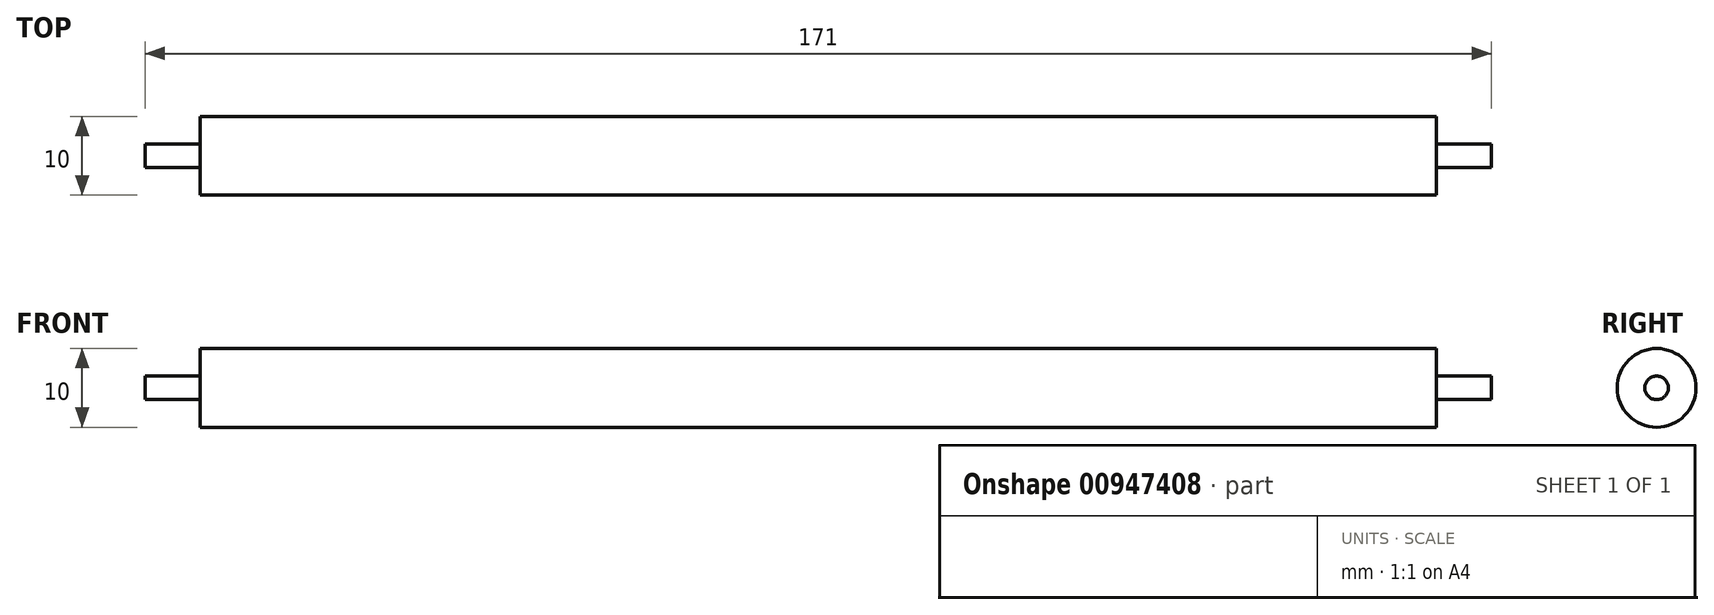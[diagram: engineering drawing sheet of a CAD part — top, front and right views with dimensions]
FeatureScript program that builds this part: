
annotation { "Feature Type Name" : "Feature", "Feature Type Description" : "" }
export const myFeature = defineFeature(function(context is Context, id is Id, definition is map)
    precondition{}
    {
        {
            var Q0;
            Q0=qCreatedBy(makeId("Right.planeOp"),FACE);
            var sketch = newSketch(context, id + "F0", { "sketchPlane" : qUnion([Q0])});
            skCircle(sketch, "E0", {"center": v(0, 0) * mm, "radius": 5 * mm});
            skSolve(sketch);
        }
        {
            var Q0;
            Q0 = qSketchRegion(id + "F0", true);
            var Q1;
            Q1=makeQuery(id+"F0.imprint","IMPRINT",FACE,{"disambiguationData":[TD([[makeQuery(id+"F0.imprint","IMPRINT",EDGE,{"derivedFrom":sQuery(id+"F0.wireOp",EDGE,"E0")}),1.0]])]});
            extrude(context, id + "F1", {"entities" : qUnion([Q0, Q1]), "depth" : 78.5 * mm, "offsetDistance" : 25.4 * mm});
        }
        {
            var Q0;
            Q0=makeQuery(id+"F1.opExtrude","CAP_FACE",FACE,{"disambiguationData":[OSD([sQuery(id+"F0.wireOp",EDGE,"E0")])],"isStart":false});
            var sketch = newSketch(context, id + "F2", { "sketchPlane" : qUnion([Q0])});
            skCircle(sketch, "E1", {"center": v(0, 0) * mm, "radius": 1.5 * mm});
            skSolve(sketch);
        }
        {
            var Q0;
            Q0=makeQuery(id+"F2.imprint","IMPRINT",FACE,{"disambiguationData":[TD([[makeQuery(id+"F2.imprint","IMPRINT",EDGE,{"derivedFrom":sQuery(id+"F2.wireOp",EDGE,"E1")}),1.0]])]});
            extrude(context, id + "F3", {"entities" : qUnion([Q0]), "operationType" : NewBodyOperationType.ADD, "depth" : 7 * mm, "offsetDistance" : 25.4 * mm});
        }
        {
            var Q0;
            Q0=makeQuery(id+"F1.opExtrude","SWEPT_BODY",BODY,{"disambiguationData":[OSD([sQuery(id+"F0.wireOp",EDGE,"E0")])]});
            var Q1;
            Q1=qCreatedBy(makeId("Right.planeOp"),FACE);
            mirror(context, id + "F4", {"operationType" : NewBodyOperationType.ADD, "entities" : qUnion([Q0]), "mirrorPlane" : qUnion([Q1])});
        }
    });
